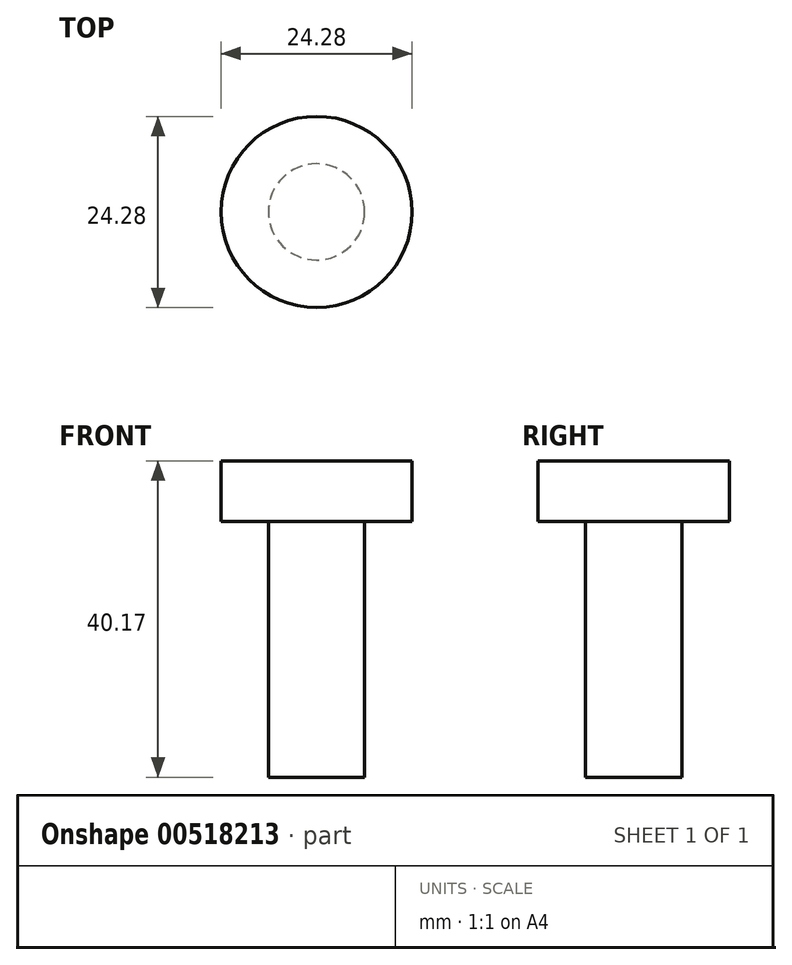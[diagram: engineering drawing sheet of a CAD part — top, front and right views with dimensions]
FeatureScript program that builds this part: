
annotation { "Feature Type Name" : "Feature", "Feature Type Description" : "" }
export const myFeature = defineFeature(function(context is Context, id is Id, definition is map)
    precondition{}
    {
        {
            var Q0;
            Q0=qCreatedBy(makeId("Front.planeOp"),FACE);
            var sketch = newSketch(context, id + "F0", { "sketchPlane" : qUnion([Q0])});
            skLineSegment(sketch, "E0", {"start": v(0, 0) * mm, "end": v(6.1, 0) * mm});
            skLineSegment(sketch, "E1", {"start": v(6.1, 0) * mm, "end": v(6.1, 32.47) * mm});
            skLineSegment(sketch, "E2", {"start": v(6.1, 32.47) * mm, "end": v(12.14, 32.47) * mm});
            skLineSegment(sketch, "E3", {"start": v(12.14, 32.47) * mm, "end": v(12.14, 40.17) * mm});
            skLineSegment(sketch, "E4", {"start": v(12.14, 40.17) * mm, "end": v(0, 40.17) * mm});
            skLineSegment(sketch, "E5", {"start": v(0, 40.17) * mm, "end": v(0, 0) * mm});
            skSolve(sketch);
        }
        {
            var Q0;
            Q0 = qSketchRegion(id + "F0", true);
            var Q1;
            Q1=sQuery(id+"F0.wireOp",EDGE,"E5");
            revolve(context, id + "F1", {"entities" : qUnion([Q0]), "axis" : qUnion([Q1]), "revolveType" : RevolveType.FULL});
        }
    });
